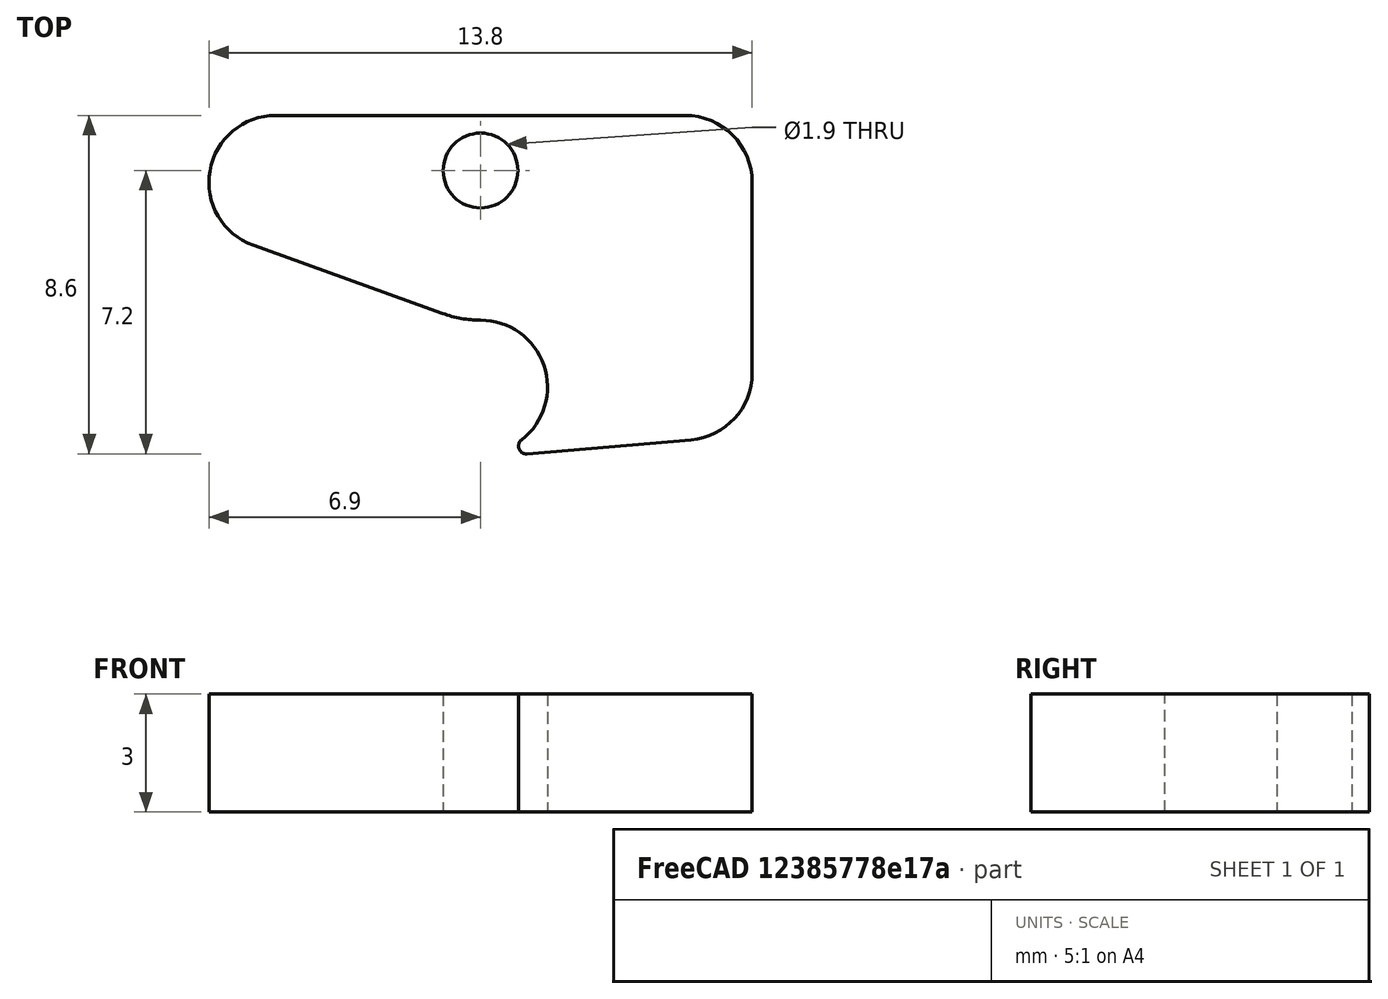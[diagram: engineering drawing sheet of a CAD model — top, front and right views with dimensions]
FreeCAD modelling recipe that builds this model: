
FCSTD DOCUMENT  (FreeCAD 1.0R39109 (Git))
Label: switchholder
License: All rights reserved
LicenseURL: http://en.wikipedia.org/wiki/All_rights_reserved
objects: Sketcher::SketchObject×1, App::VarSet×1, PartDesign::Pad×1, PartDesign::Body×1
note: 6 computed .brp shape members not serialized (recipe doc carries the construction recipe); baked Part::Feature solids carry a one-line shape summary decoded from their .brp

FEATURE [Sketcher::SketchObject] Sketch
  ArcFitTolerance = 1e-06
  AttachmentSupport = -> [XY_Plane]
  FullyConstrained = true
  MakeInternals = false
  MapMode = 5
  expr: Constraints[16] = VarSet.cent_pin_diam / 2 + VarSet.tolerance
  expr: Constraints[18] = VarSet.switch_width
  expr: Constraints[21] = VarSet.support_pin_diam + VarSet.tolerance
  expr: Constraints[22] = VarSet.cent_to_support
  expr: Constraints[23] = VarSet.switch_width / 2
  expr: Constraints[24] = VarSet.switch_width / 2
  expr: Constraints[25] = VarSet.tolerance * 2
  sketch-geometry (13):
    g0: ArcOfCircle CenterX=0 CenterY=0 CenterZ=0 NormalX=0 NormalY=0 NormalZ=1 AngleXU=0 Radius=1.7 StartAngle=5.37261 EndAngle=7.85398
    g1: ArcOfCircle [constr] CenterX=0 CenterY=0 CenterZ=0 NormalX=0 NormalY=0 NormalZ=1 AngleXU=0 Radius=1.7 StartAngle=4.71239 EndAngle=5.37261
    g2: ArcOfCircle CenterX=1.16525 CenterY=-1.50073 CenterZ=0 NormalX=0 NormalY=0 NormalZ=1 AngleXU=0 Radius=0.2 StartAngle=2.23101 EndAngle=4.79799
    g3: LineSegment StartX=1.18235 StartY=-1.7 StartZ=0 EndX=5.34535 EndY=-1.34276 EndZ=0
    g4: ArcOfCircle CenterX=5.2 CenterY=0.351015 CenterZ=0 NormalX=0 NormalY=0 NormalZ=1 AngleXU=0 Radius=1.7 StartAngle=4.79799 EndAngle=6.28319
    g5: LineSegment StartX=6.9 StartY=0.351015 StartZ=0 EndX=6.9 EndY=5.2 EndZ=0
    g6: ArcOfCircle CenterX=5.2 CenterY=5.2 CenterZ=0 NormalX=0 NormalY=0 NormalZ=1 AngleXU=0 Radius=1.7 StartAngle=1e-16 EndAngle=1.5708
    g7: LineSegment StartX=5.2 StartY=6.9 StartZ=0 EndX=-5.2 EndY=6.9 EndZ=0
    g8: ArcOfCircle CenterX=-5.2 CenterY=5.2 CenterZ=0 NormalX=0 NormalY=0 NormalZ=1 AngleXU=0 Radius=1.7 StartAngle=1.5708 EndAngle=4.36679
    g9: LineSegment StartX=-5.7759 StartY=3.60052 StartZ=0 EndX=-0.965474 EndY=1.86852 EndZ=0
    g10: GeomPoint X=-6.9 Y=5.2 Z=0
    g11: Circle CenterX=0 CenterY=5.5 CenterZ=0 NormalX=0 NormalY=0 NormalZ=1 AngleXU=0 Radius=0.95
    g12: ArcOfCircle CenterX=-3e-16 CenterY=4.55 CenterZ=0 NormalX=0 NormalY=0 NormalZ=1 AngleXU=0 Radius=2.85 StartAngle=4.36679 EndAngle=4.71239
  constraints (33):
    c: Coincident(g0,g-1)
    c: PointOnObject(g0,g-2)
    c: Coincident(g1,g0)
    c: Coincident(g1,g0)
    c: PointOnObject(g1,g-2)
    c: Tangent(g2,g0) = 1.5708
    c: Tangent(g3,g2) = -1.5708
    c: Tangent(g4,g3) = -1.5708
    c: Vertical(g5)
    c: Tangent(g5,g4) = -1.5708
    c: Tangent(g5,g6) = -1.5708
    c: Tangent(g6,g7) = -1.5708
    c: Horizontal(g7)
    c: Tangent(g7,g8) = -1.5708
    c: Tangent(g8,g9) = -1.5708
    c: Horizontal(g2,g1)
    c: Radius(g0) = 1.7
    c: Horizontal(g10,g8)
    c: DistanceX(g10,g5) = 13.8
    c: PointOnObject(g10,g8)
    c: PointOnObject(g11,g-2)
    c: Diameter(g11) = 1.9
    c: DistanceY(g0,g11) = 5.5
    c: DistanceX(g0,g5) = 6.9
    c: DistanceY(g0,g6) = 6.9
    c: Radius(g2) = 0.2
    c: Equal(g8,g6)
    c: Tangent(g12,g0) = 1.5708
    c: Horizontal(g3,g0)
    c: Tangent(g9,g12) = -1.5708
    c: PointOnObject(g12,g11)
    c: Equal(g4,g6)
    c: Equal(g6,g0)
FEATURE [App::VarSet] VarSet
  cent_pin_diam = 3.2
  cent_to_support = 5.5
  support_pin_diam = 1.8
  switch_width = 13.8
  tolerance = 0.1
FEATURE [PartDesign::Pad] Pad
  Direction = (0,0,1)
  Length = 3
  Length2 = 10
  Profile = -> Sketch
  ReferenceAxis = -> Sketch [N_Axis]
  Refine = true
  Suppressed = false
  Type = 0
FEATURE [PartDesign::Body] Body
  AllowCompound = false
  Group = -> [VarSet,Sketch,Pad]
  Origin = -> Origin
  Tip = -> Pad
